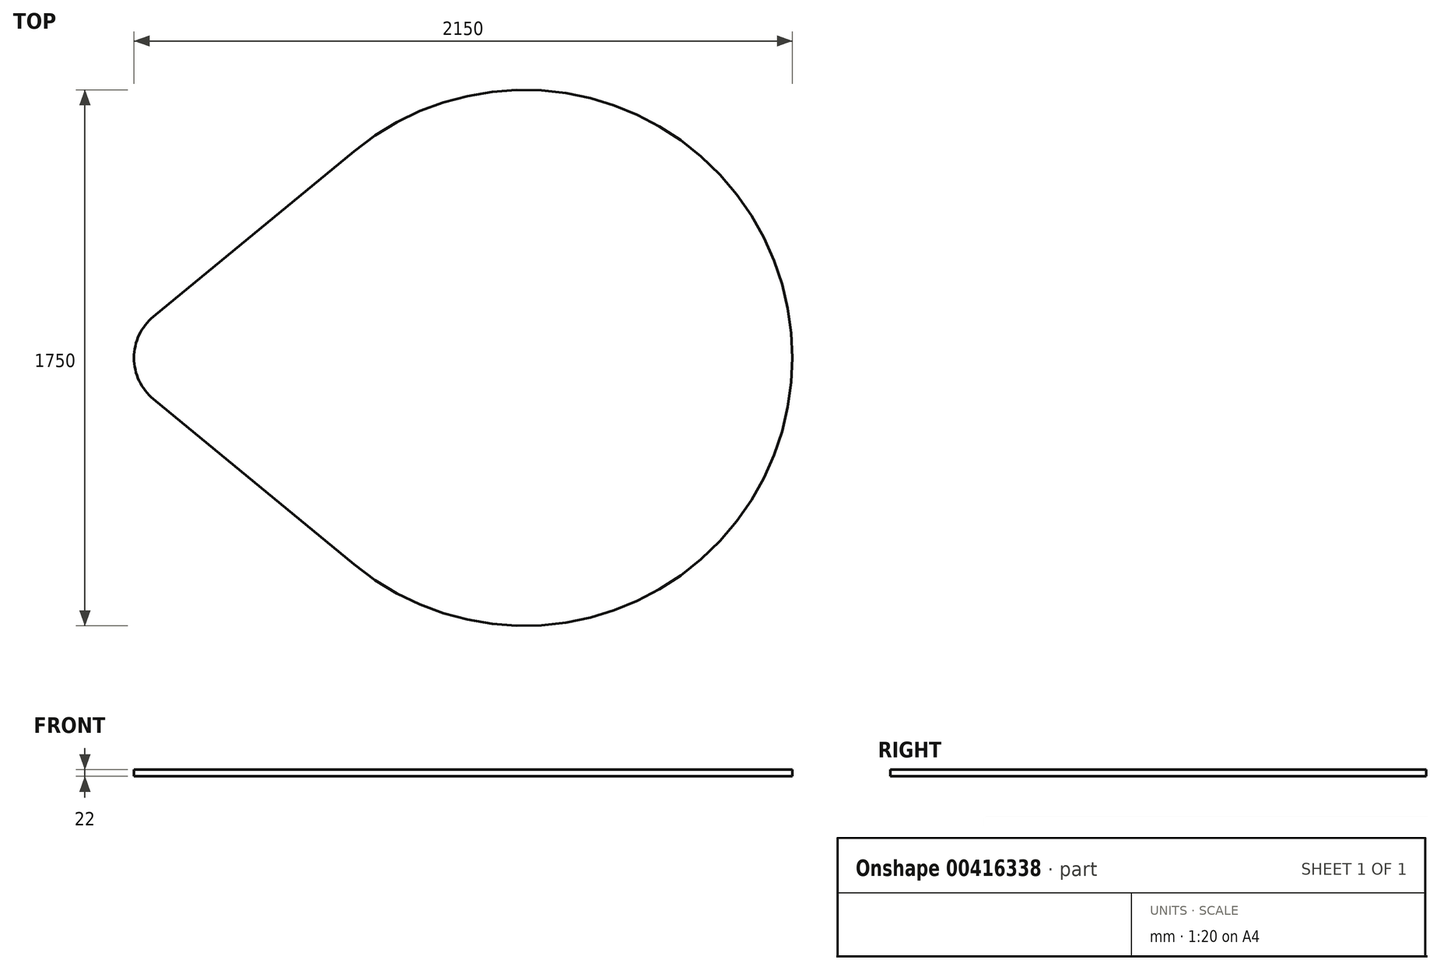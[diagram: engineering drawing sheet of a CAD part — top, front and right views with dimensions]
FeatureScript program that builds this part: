
annotation { "Feature Type Name" : "Feature", "Feature Type Description" : "" }
export const myFeature = defineFeature(function(context is Context, id is Id, definition is map)
    precondition{}
    {
        {
            var Q0;
            Q0=qCreatedBy(makeId("Top.planeOp"),FACE);
            var sketch = newSketch(context, id + "F0", { "sketchPlane" : qUnion([Q0])});
            skArc(sketch, "E0", {"start": v(875, 0) * mm, "mid": v(373.1, 791.47) * mm, "end": v(-556.82, 674.97) * mm});
            skLineSegment(sketch, "E1", {"start": v(0, 0) * mm, "end": v(-1100, 0) * mm});
            skArc(sketch, "E2", {"start": v(-1211.36, 135) * mm, "mid": v(-1258.3, 74.62) * mm, "end": v(-1275, 0) * mm});
            skLineSegment(sketch, "E3", {"start": v(-1100, 0) * mm, "end": v(-1275, 0) * mm});
            skLineSegment(sketch, "E4", {"start": v(-1211.36, 135) * mm, "end": v(-556.82, 674.97) * mm});
            skPoint(sketch, "E5", {"position": v(-875, 0) * mm});
            skLineSegment(sketch, "E6", {"start": v(0, 0) * mm, "end": v(875, 0) * mm});
            skSolve(sketch);
        }
        {
            var Q0;
            Q0 = qSketchRegion(id + "F0", true);
            extrude(context, id + "F1", {"entities" : qUnion([Q0]), "oppositeDirection" : true, "depth" : 22 * mm});
        }
        {
            var Q0;
            Q0=makeQuery(id+"F1.opExtrude","SWEPT_BODY",BODY,{"disambiguationData":[OSD([sQuery(id+"F0.wireOp",EDGE,"E0"),sQuery(id+"F0.wireOp",EDGE,"E1"),sQuery(id+"F0.wireOp",EDGE,"E2"),sQuery(id+"F0.wireOp",EDGE,"E3"),sQuery(id+"F0.wireOp",EDGE,"E4"),sQuery(id+"F0.wireOp",EDGE,"E6")])]});
            var Q1;
            Q1=qCreatedBy(makeId("Front.planeOp"),FACE);
            mirror(context, id + "F2", {"operationType" : NewBodyOperationType.ADD, "entities" : qUnion([Q0]), "mirrorPlane" : qUnion([Q1])});
        }
    });
